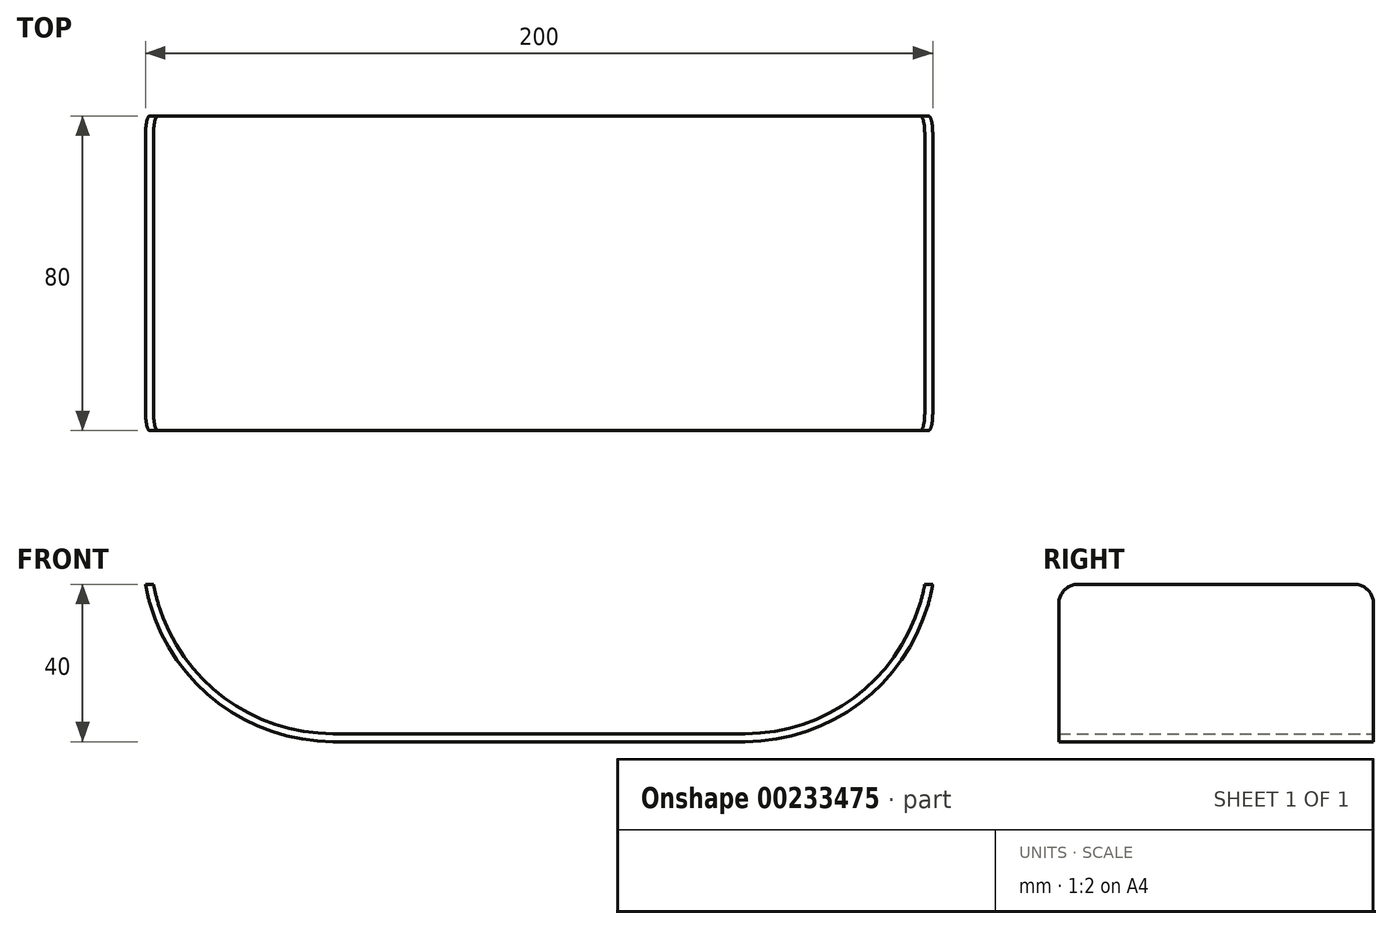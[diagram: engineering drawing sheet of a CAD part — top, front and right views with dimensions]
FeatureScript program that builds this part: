
annotation { "Feature Type Name" : "Feature", "Feature Type Description" : "" }
export const myFeature = defineFeature(function(context is Context, id is Id, definition is map)
    precondition{}
    {
        {
            var Q0;
            Q0=qCreatedBy(makeId("Front.planeOp"),FACE);
            var sketch = newSketch(context, id + "F0", { "sketchPlane" : qUnion([Q0])});
            skLineSegment(sketch, "E0", {"start": v(0, 0) * mm, "end": v(-52.33, 0) * mm});
            skLineSegment(sketch, "E1", {"start": v(-100, 40) * mm, "end": v(-103.8, 61.59) * mm, "construction": true});
            skArc(sketch, "E2", {"start": v(-52.33, 0) * mm, "mid": v(-83.44, 11.32) * mm, "end": v(-100, 40) * mm});
            skLineSegment(sketch, "E3", {"start": v(0, 0) * mm, "end": v(0, 20.65) * mm, "construction": true});
            skArc(sketch, "E4.0", {"start": v(-52.33, 2) * mm, "mid": v(-82.02, 12.74) * mm, "end": v(-97.97, 40) * mm});
            skLineSegment(sketch, "E4.1", {"start": v(0, 2) * mm, "end": v(-52.33, 2) * mm});
            skLineSegment(sketch, "E5", {"start": v(-100, 40) * mm, "end": v(-97.97, 40) * mm});
            skLineSegment(sketch, "E6", {"start": v(0, 2) * mm, "end": v(0, 0) * mm});
            skLineSegment(sketch, "E7", {"start": v(0, -0.7) * mm, "end": v(0, 28.32) * mm, "construction": true});
            skLineSegment(sketch, "E8.MirrorCS", {"start": v(0, 2) * mm, "end": v(52.33, 2) * mm, "construction": true});
            skArc(sketch, "E9.MirrorCS", {"start": v(52.33, 2) * mm, "mid": v(82.02, 12.74) * mm, "end": v(97.97, 40) * mm, "construction": true});
            skArc(sketch, "E10.MirrorCS", {"start": v(52.33, 0) * mm, "mid": v(83.44, 11.32) * mm, "end": v(100, 40) * mm, "construction": true});
            skLineSegment(sketch, "E11.MirrorCS", {"start": v(0, 0) * mm, "end": v(52.33, 0) * mm, "construction": true});
            skLineSegment(sketch, "E12.MirrorCS", {"start": v(100, 40) * mm, "end": v(97.97, 40) * mm, "construction": true});
            skLineSegment(sketch, "E13", {"start": v(0, 2) * mm, "end": v(0, 0) * mm, "construction": true});
            skSolve(sketch);
        }
        {
            var Q0;
            Q0 = qSketchRegion(id + "F0", true);
            extrude(context, id + "F1", {"entities" : qUnion([Q0]), "offsetDistance" : 25 * mm, "depth" : 80 * mm});
        }
        {
            var Q0;
            Q0=makeQuery(id+"F1.opExtrude","SWEPT_BODY",BODY,{"disambiguationData":[OSD([sQuery(id+"F0.wireOp",EDGE,"E0"),sQuery(id+"F0.wireOp",EDGE,"E2"),sQuery(id+"F0.wireOp",EDGE,"E4.0"),sQuery(id+"F0.wireOp",EDGE,"E4.1"),sQuery(id+"F0.wireOp",EDGE,"E5"),sQuery(id+"F0.wireOp",EDGE,"E6")])]});
            var Q1;
            Q1=makeQuery(id+"F1.opExtrude","SWEPT_FACE",FACE,{"disambiguationData":[OSD([sQuery(id+"F0.wireOp",EDGE,"E6")])]});
            mirror(context, id + "F2", {"operationType" : NewBodyOperationType.ADD, "entities" : qUnion([Q0]), "mirrorPlane" : qUnion([Q1])});
        }
        {
            var Q0;
            Q0=makeQuery(id+"F1.opExtrude","CAP_EDGE",EDGE,{"disambiguationData":[OSD([sQuery(id+"F0.wireOp",EDGE,"E5")])],"isStart":false});
            var Q1;
            Q1=makeQuery(id+"F1.opExtrude","CAP_EDGE",EDGE,{"disambiguationData":[OSD([sQuery(id+"F0.wireOp",EDGE,"E5")])],"isStart":true});
            var Q2;
            Q2=makeQuery(id+"F2.opPattern","COPY",EDGE,{"derivedFrom":makeQuery(id+"F1.opExtrude","CAP_EDGE",EDGE,{"disambiguationData":[OSD([sQuery(id+"F0.wireOp",EDGE,"E5")])],"isStart":false}),"instanceName":"1"});
            var Q3;
            Q3=makeQuery(id+"F2.opPattern","COPY",EDGE,{"derivedFrom":makeQuery(id+"F1.opExtrude","CAP_EDGE",EDGE,{"disambiguationData":[OSD([sQuery(id+"F0.wireOp",EDGE,"E5")])],"isStart":true}),"instanceName":"1"});
            fillet(context, id + "F3", {"entities" : qUnion([Q0, Q1, Q2, Q3]), "radius" : 5 * mm, "tangentPropagation" : true, "defaultsChanged" : false, "vertexSettings" : [], "allowEdgeOverflow" : false});
        }
    });
